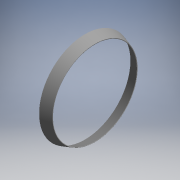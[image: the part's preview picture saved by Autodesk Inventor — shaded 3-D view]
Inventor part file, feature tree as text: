
AUTODESK INVENTOR PART (.ipt)
format: ipt  version: 2017.3 (Build 213256000, 256)  size: 212,992 bytes
history: native  units: mm (DEFAULTED — no unit token found)
features: other x266, revolve x1, sketch x1
ambient origin geometry x8: Origin, YZ Plane, XZ Plane, XY Plane, X Axis, Y Axis, Z Axis, Center Point
bodies: Solid1 (feature_tree)
feature tree (268):
  revolve  "Revolution1"  [1 undecoded]
  other  "cage_XY"
  other  "cage_YZ"
  other  "cage_ZX"
  other  "cage_X"
  other  "cage_Y"
  other  "cage_Z"
  other  "cage_Center"
  other  "roller1_XY"
  other  "roller1_YZ"
  other  "roller1_ZX"
  other  "roller1_X"
  other  "roller1_Y"
  other  "roller1_Z"
  other  "roller1_Center"
  other  "roller10_XY"
  other  "roller10_YZ"
  other  "roller10_ZX"
  other  "roller10_X"
  other  "roller10_Y"
  other  "roller10_Z"
  other  "roller10_Center"
  other  "roller11_XY"
  other  "roller11_YZ"
  other  "roller11_ZX"
  other  "roller11_X"
  other  "roller11_Y"
  other  "roller11_Z"
  other  "roller11_Center"
  other  "roller12_XY"
  other  "roller12_YZ"
  other  "roller12_ZX"
  other  "roller12_X"
  other  "roller12_Y"
  other  "roller12_Z"
  other  "roller12_Center"
  other  "roller13_XY"
  other  "roller13_YZ"
  other  "roller13_ZX"
  other  "roller13_X"
  other  "roller13_Y"
  other  "roller13_Z"
  other  "roller13_Center"
  other  "roller14_XY"
  other  "roller14_YZ"
  other  "roller14_ZX"
  other  "roller14_X"
  other  "roller14_Y"
  other  "roller14_Z"
  other  "roller14_Center"
  other  "roller15_XY"
  other  "roller15_YZ"
  other  "roller15_ZX"
  other  "roller15_X"
  other  "roller15_Y"
  other  "roller15_Z"
  other  "roller15_Center"
  other  "roller16_XY"
  other  "roller16_YZ"
  other  "roller16_ZX"
  other  "roller16_X"
  other  "roller16_Y"
  other  "roller16_Z"
  other  "roller16_Center"
  other  "roller17_XY"
  other  "roller17_YZ"
  other  "roller17_ZX"
  other  "roller17_X"
  other  "roller17_Y"
  other  "roller17_Z"
  other  "roller17_Center"
  other  "roller18_XY"
  other  "roller18_YZ"
  other  "roller18_ZX"
  other  "roller18_X"
  other  "roller18_Y"
  other  "roller18_Z"
  other  "roller18_Center"
  other  "roller19_XY"
  other  "roller19_YZ"
  other  "roller19_ZX"
  other  "roller19_X"
  other  "roller19_Y"
  other  "roller19_Z"
  other  "roller19_Center"
  other  "roller2_XY"
  other  "roller2_YZ"
  other  "roller2_ZX"
  other  "roller2_X"
  other  "roller2_Y"
  other  "roller2_Z"
  other  "roller2_Center"
  other  "roller20_XY"
  other  "roller20_YZ"
  other  "roller20_ZX"
  other  "roller20_X"
  other  "roller20_Y"
  other  "roller20_Z"
  other  "roller20_Center"
  other  "roller21_XY"
  other  "roller21_YZ"
  other  "roller21_ZX"
  other  "roller21_X"
  other  "roller21_Y"
  other  "roller21_Z"
  other  "roller21_Center"
  other  "roller22_XY"
  other  "roller22_YZ"
  other  "roller22_ZX"
  other  "roller22_X"
  other  "roller22_Y"
  other  "roller22_Z"
  other  "roller22_Center"
  other  "roller23_XY"
  other  "roller23_YZ"
  other  "roller23_ZX"
  other  "roller23_X"
  other  "roller23_Y"
  other  "roller23_Z"
  other  "roller23_Center"
  other  "roller24_XY"
  other  "roller24_YZ"
  other  "roller24_ZX"
  other  "roller24_X"
  other  "roller24_Y"
  other  "roller24_Z"
  other  "roller24_Center"
  other  "roller25_XY"
  other  "roller25_YZ"
  other  "roller25_ZX"
  other  "roller25_X"
  other  "roller25_Y"
  other  "roller25_Z"
  other  "roller25_Center"
  other  "roller26_XY"
  other  "roller26_YZ"
  other  "roller26_ZX"
  other  "roller26_X"
  other  "roller26_Y"
  other  "roller26_Z"
  other  "roller26_Center"
  other  "roller27_XY"
  other  "roller27_YZ"
  other  "roller27_ZX"
  other  "roller27_X"
  other  "roller27_Y"
  other  "roller27_Z"
  other  "roller27_Center"
  other  "roller28_XY"
  other  "roller28_YZ"
  other  "roller28_ZX"
  other  "roller28_X"
  other  "roller28_Y"
  other  "roller28_Z"
  other  "roller28_Center"
  other  "roller29_XY"
  other  "roller29_YZ"
  other  "roller29_ZX"
  other  "roller29_X"
  other  "roller29_Y"
  other  "roller29_Z"
  other  "roller29_Center"
  other  "roller3_XY"
  other  "roller3_YZ"
  other  "roller3_ZX"
  other  "roller3_X"
  other  "roller3_Y"
  other  "roller3_Z"
  other  "roller3_Center"
  other  "roller30_XY"
  other  "roller30_YZ"
  other  "roller30_ZX"
  other  "roller30_X"
  other  "roller30_Y"
  other  "roller30_Z"
  other  "roller30_Center"
  other  "roller31_XY"
  other  "roller31_YZ"
  other  "roller31_ZX"
  other  "roller31_X"
  other  "roller31_Y"
  other  "roller31_Z"
  other  "roller31_Center"
  other  "roller32_XY"
  other  "roller32_YZ"
  other  "roller32_ZX"
  other  "roller32_X"
  other  "roller32_Y"
  other  "roller32_Z"
  other  "roller32_Center"
  other  "roller33_XY"
  other  "roller33_YZ"
  other  "roller33_ZX"
  other  "roller33_X"
  other  "roller33_Y"
  other  "roller33_Z"
  other  "roller33_Center"
  other  "roller34_XY"
  other  "roller34_YZ"
  other  "roller34_ZX"
  other  "roller34_X"
  other  "roller34_Y"
  other  "roller34_Z"
  other  "roller34_Center"
  other  "roller35_XY"
  other  "roller35_YZ"
  other  "roller35_ZX"
  other  "roller35_X"
  other  "roller35_Y"
  other  "roller35_Z"
  other  "roller35_Center"
  other  "roller36_XY"
  other  "roller36_YZ"
  other  "roller36_ZX"
  other  "roller36_X"
  other  "roller36_Y"
  other  "roller36_Z"
  other  "roller36_Center"
  other  "roller37_XY"
  other  "roller37_YZ"
  other  "roller37_ZX"
  other  "roller37_X"
  other  "roller37_Y"
  other  "roller37_Z"
  other  "roller37_Center"
  other  "roller4_XY"
  other  "roller4_YZ"
  other  "roller4_ZX"
  other  "roller4_X"
  other  "roller4_Y"
  other  "roller4_Z"
  other  "roller4_Center"
  other  "roller5_XY"
  other  "roller5_YZ"
  other  "roller5_ZX"
  other  "roller5_X"
  other  "roller5_Y"
  other  "roller5_Z"
  other  "roller5_Center"
  other  "roller6_XY"
  other  "roller6_YZ"
  other  "roller6_ZX"
  other  "roller6_X"
  other  "roller6_Y"
  other  "roller6_Z"
  other  "roller6_Center"
  other  "roller7_XY"
  other  "roller7_YZ"
  other  "roller7_ZX"
  other  "roller7_X"
  other  "roller7_Y"
  other  "roller7_Z"
  other  "roller7_Center"
  other  "roller8_XY"
  other  "roller8_YZ"
  other  "roller8_ZX"
  other  "roller8_X"
  other  "roller8_Y"
  other  "roller8_Z"
  other  "roller8_Center"
  other  "roller9_XY"
  other  "roller9_YZ"
  other  "roller9_ZX"
  other  "roller9_X"
  other  "roller9_Y"
  other  "roller9_Z"
  other  "roller9_Center"
  sketch  "Sketch_1"  dims[d0=360.0deg]
note: 1 required parameter value undecoded (feature->parameter linkage not recoverable at this tier; creation-order binding heuristic only, values carry confidence <= 0.55)
